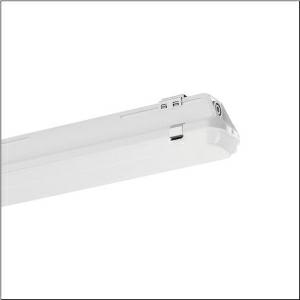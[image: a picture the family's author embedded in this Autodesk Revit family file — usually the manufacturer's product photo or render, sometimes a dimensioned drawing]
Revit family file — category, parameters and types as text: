
# Revit family: monsun_r__21_parking_51fg20dp440b_2f1b
name_source: partatom
category: Lighting Fixtures
units: mm (PartAtom-declared; Revit-internal decimal feet)

## family parameters
Cut with Voids When Loaded = No
Host = Face
Light Source = No
Part Type = Normal
Room Calculation Point = No
Round Connector Dimension = Use Diameter
Shared = No

## types (1)
- --- (1 x LED, 4810 lm, 34.4 W, 4000K)
    Apparent Load = 34 VA
    CIE Flux Codes = 45 75 93 94 100
    Color Rendering = 80
    Color Temperature = 4000K
    Default Elevation = 1800 mm
    Description = Monsun® 21 parking, damp-proof luminaire, chain hanger, primary optical cover: enclosure, of PC, light emission: direct distribution, primary light characteristic: symmetric, installation type: suspended mounting, surface-mounted, horizontal mounting, vertical mounting, LED, rated luminous flux: 4.810lm, luminous efficacy: 140lm/W, light colour: 840, colour temperature: 4000K, control gear: ECG DALI, with terminal, 5-pole, max. 2.5mm², mains connection: 220..240V, AC, 50/60Hz, rated input power: 34W, housing, of glass-fibre reinforced polyester, uncoated, bright grey, length: 1.590mm, width: 90mm, height: 88mm, clip for enclosure, of stainless steel (V2A), ceiling mounting element, of stainless steel (V2A), chain hanger, of stainless steel (V2A), protection rating (complete): IP66, insulation class (complete): insulation class I (protective earthing), certification: CE, ENEC, VDE, UKCA, protection symbol: D, impact resistance: IK08, permissible operating ambient temperature: -25..+35°C, standard: EN 50419, EN 60598-2-1, corresponds to IFS (International Featured Standards) requirements for safety and quality in the food industry, for indoor or canopied outdoor use, no direct snow, no direct sun, no direct rain, packaging unit: 1 piece
    Height = 89 mm
    Lamp = 1 x LED
    Lamp Light Flux = 4810 lm
    Lamp Power = 34.4 W
    Lamp count = 1
    Length = 1590 mm
    Luminous efficacy = 140 lm/W
    Manufacturer = Siteco
    ModVariant = No
    Model = 51FG20DP440B
    Mounting Place = Ceiling
    Mounting Type = Pendant
    Number of Poles = 1
    OnlyDefault = Yes
    Power Factor = 1
    Product Name = Monsun® 21 parking
    Product group = damp-proof luminaire | ceiling pendant
    ProductGroupID = 908
    Protection Class = Protection class I
    Protection Degree = IP 66
    RLX_Detail_Level = 1
    RlxData = <blob elided: 91761 chars, md5=bc066481>
    Socket = socket
    Standby Power = 0 W
    System Light Flux = 4810 lm
    System Power = 34 W
    Type Comments = factory setting: luminous flux: 100 % | dim-lin: 254 | 228 mA
    Type Image = l_1006717.jpg
    URL = http://relux.com
    VarID = @adj_124971
    Voltage = 0 V
    Weight = 0.00 kg
    Width = 90 mm

## geometry (parser evidence)
native form markers: Blend x4, Sweep x13
no freeform markers — native parametric forms only
